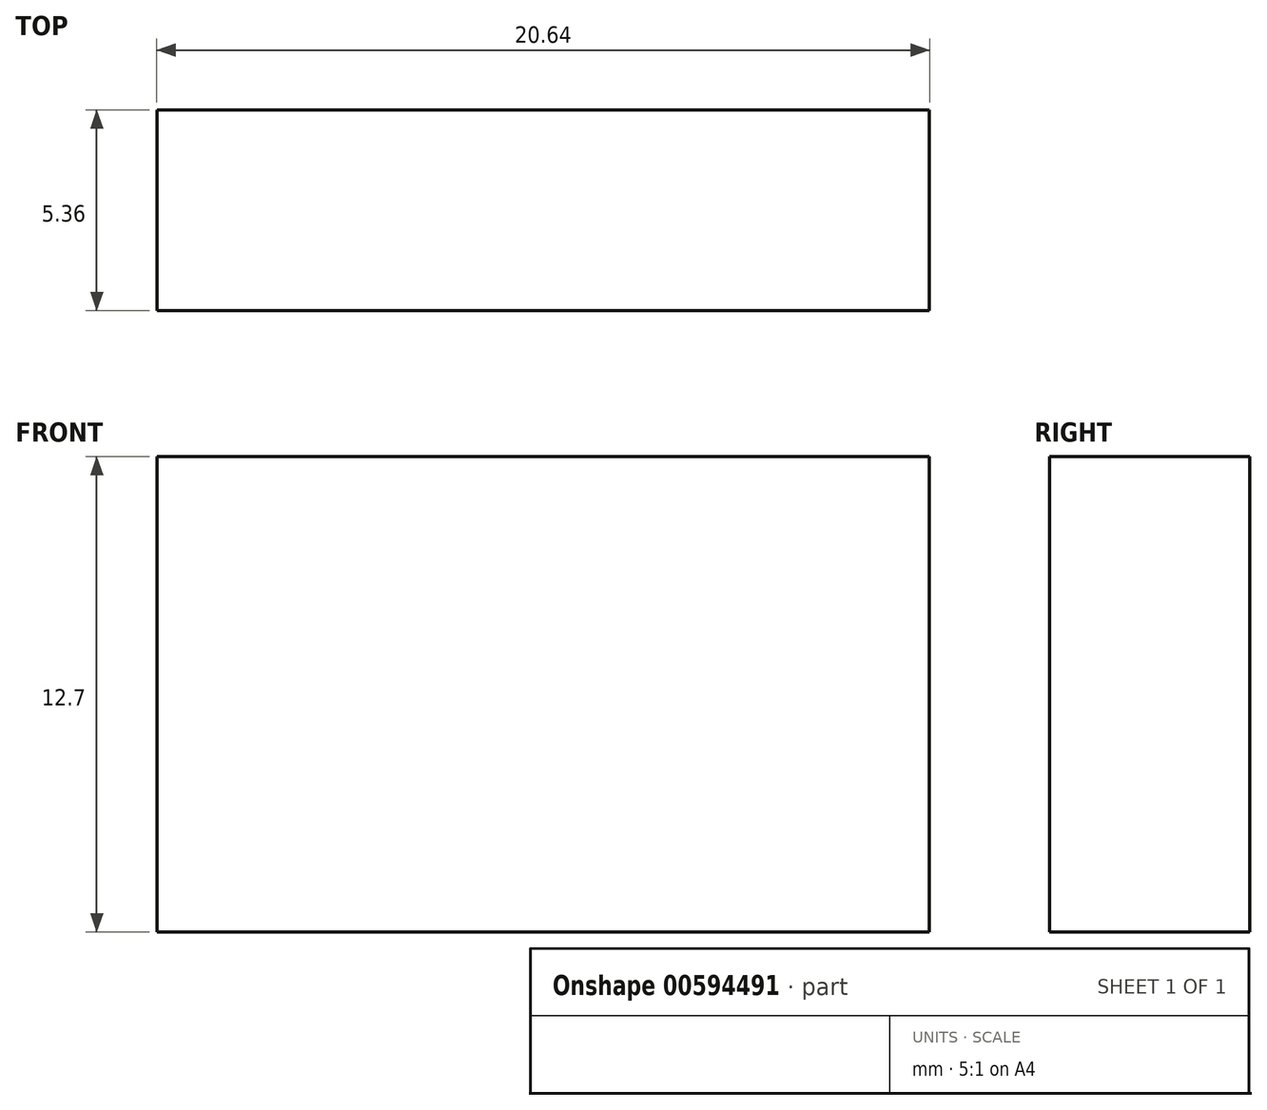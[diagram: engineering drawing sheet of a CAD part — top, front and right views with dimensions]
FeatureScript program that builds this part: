
annotation { "Feature Type Name" : "Feature", "Feature Type Description" : "" }
export const myFeature = defineFeature(function(context is Context, id is Id, definition is map)
    precondition{}
    {
        {
            var Q0;
            Q0=qCreatedBy(makeId("Top.planeOp"),FACE);
            var sketch = newSketch(context, id + "F0", { "sketchPlane" : qUnion([Q0])});
            skLineSegment(sketch, "E0", {"start": v(-10.32, 2.68) * mm, "end": v(10.32, 2.68) * mm});
            skLineSegment(sketch, "E1", {"start": v(10.32, 2.68) * mm, "end": v(10.32, -2.68) * mm});
            skLineSegment(sketch, "E2", {"start": v(10.32, -2.68) * mm, "end": v(-10.32, -2.68) * mm});
            skLineSegment(sketch, "E3", {"start": v(-10.32, -2.68) * mm, "end": v(-10.32, 2.68) * mm});
            skSolve(sketch);
        }
        {
            var Q0;
            Q0 = qSketchRegion(id + "F0", true);
            extrude(context, id + "F1", {"entities" : qUnion([Q0]), "depth" : 12.7 * mm, "offsetDistance" : 25.4 * mm});
        }
    });
